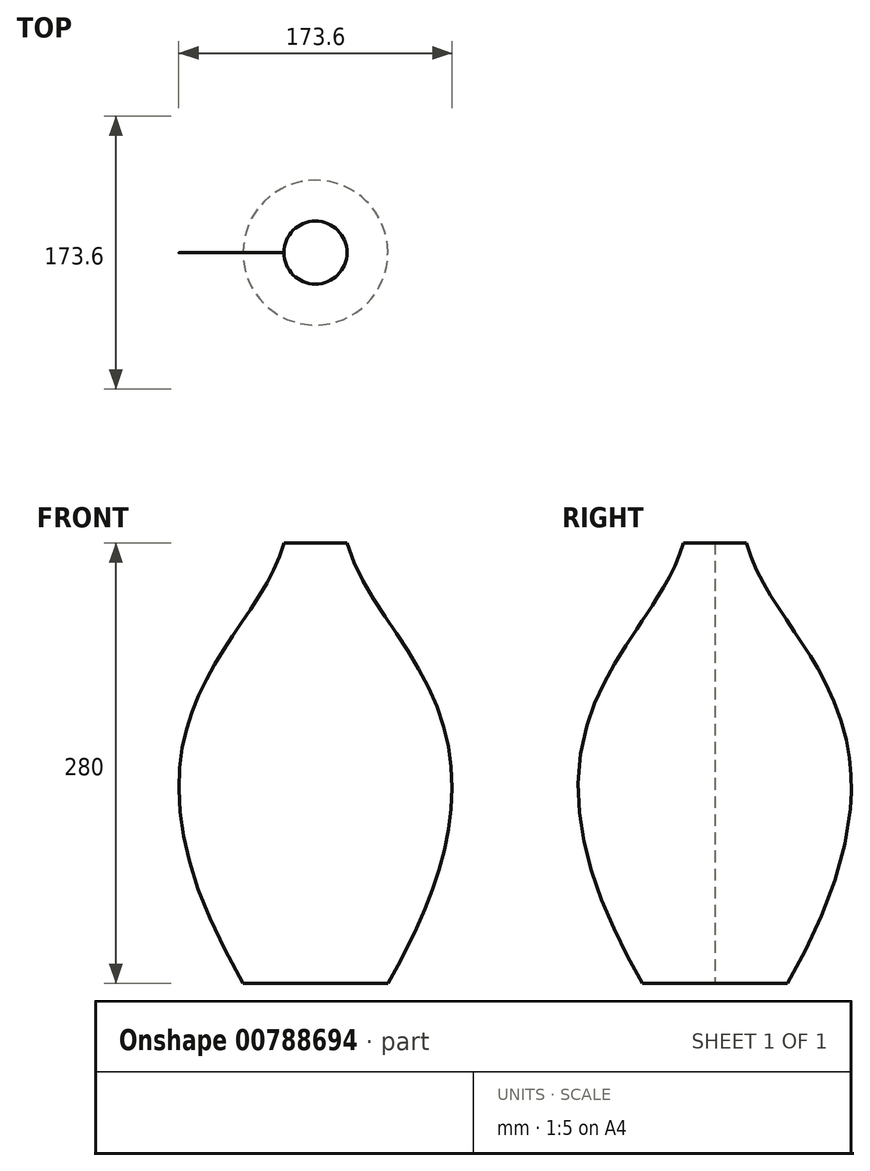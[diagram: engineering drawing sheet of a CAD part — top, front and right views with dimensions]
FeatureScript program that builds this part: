
annotation { "Feature Type Name" : "Feature", "Feature Type Description" : "" }
export const myFeature = defineFeature(function(context is Context, id is Id, definition is map)
    precondition{}
    {
        {
            var Q0;
            Q0=qCreatedBy(makeId("Front.planeOp"),FACE);
            var sketch = newSketch(context, id + "F0", { "sketchPlane" : qUnion([Q0])});
            skLineSegment(sketch, "E0", {"start": v(0, 0) * mm, "end": v(0, 280) * mm});
            skLineSegment(sketch, "E1", {"start": v(0, 0) * mm, "end": v(46, 0) * mm});
            skLineSegment(sketch, "E2", {"start": v(0, 280) * mm, "end": v(20, 280) * mm});
            skLineSegment(sketch, "E3", {"start": v(46, 0) * mm, "end": v(46, 241.11) * mm, "construction": true});
            skPoint(sketch, "E4", {"position": v(46, 225) * mm});
            skLineSegment(sketch, "E5", {"start": v(46, 0) * mm, "end": v(321.26, 476.76) * mm, "construction": true});
            skLineSegment(sketch, "E6", {"start": v(20, 280) * mm, "end": v(-150.18, 109.82) * mm, "construction": true});
            skLineSegment(sketch, "E7", {"start": v(83.32, 0) * mm, "end": v(83.32, 280) * mm, "construction": true});
            skFitSpline(sketch, "E8", {"points": [v(20, 280) * mm, v(46, 0) * mm], "startDerivative": vector(54.31, -203.23) * mm, "endDerivative": vector(-292.3, -506.28) * mm});
            skSolve(sketch);
        }
        {
            var Q0;
            Q0=makeQuery(id+"F0.imprint","IMPRINT",FACE,{"disambiguationData":[TD([[makeQuery(id+"F0.imprint","IMPRINT",EDGE,{"derivedFrom":sQuery(id+"F0.wireOp",EDGE,"E0")}),-1.0]])]});
            var Q1;
            Q1=sQuery(id+"F0.wireOp",EDGE,"E0");
            revolve(context, id + "F1", {"surfaceOperationType" : NewSurfaceOperationType.NEW, "entities" : qUnion([Q0]), "axis" : qUnion([Q1]), "revolveType" : RevolveType.FULL});
        }
    });
